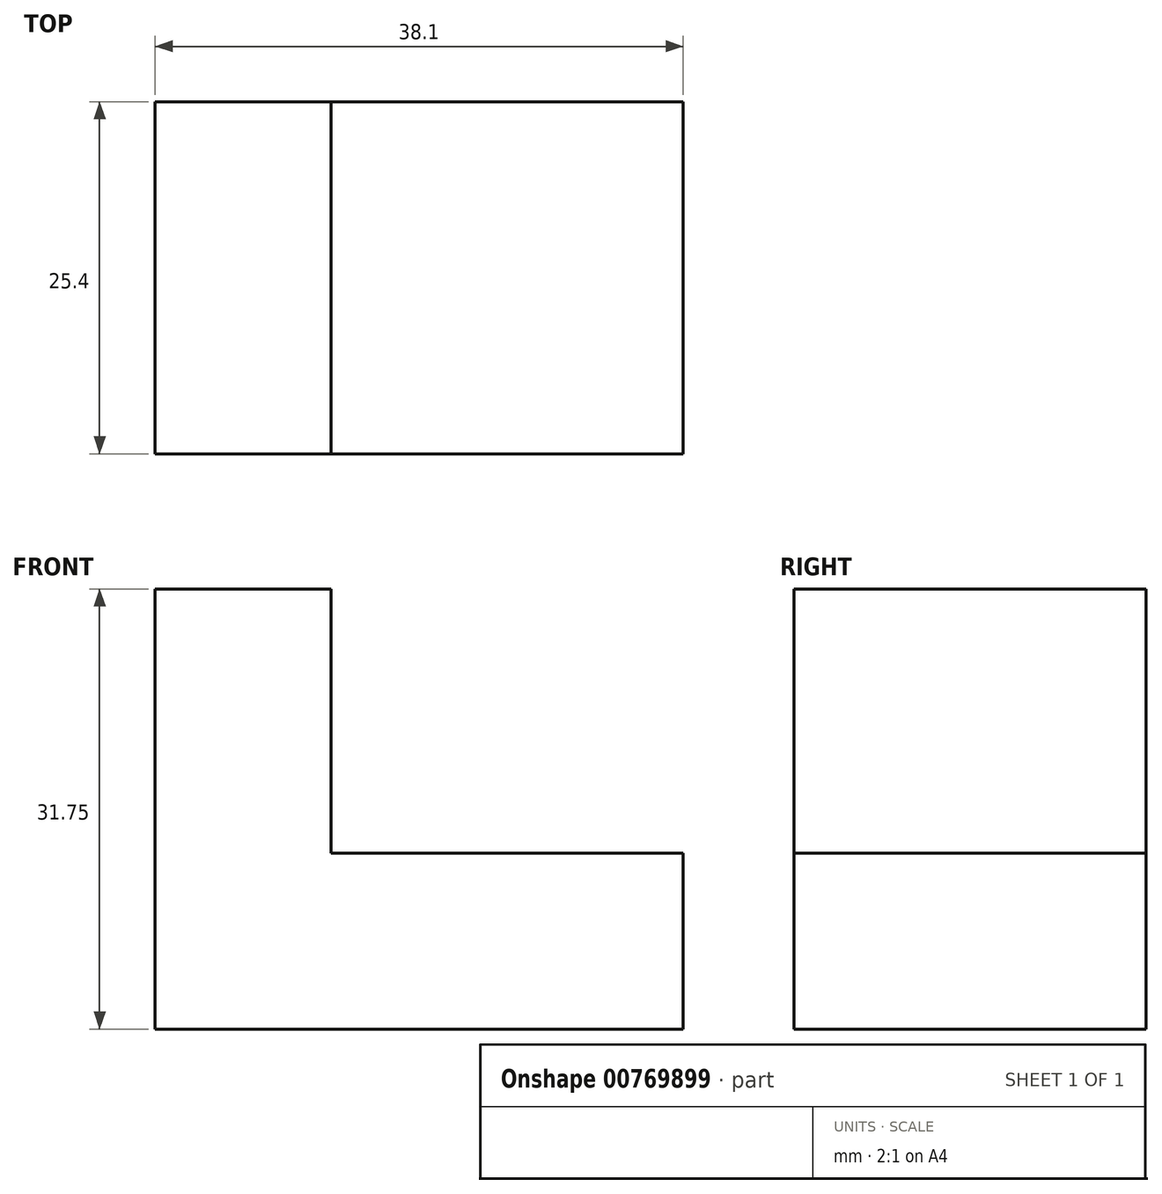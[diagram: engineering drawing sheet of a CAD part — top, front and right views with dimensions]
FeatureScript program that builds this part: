
annotation { "Feature Type Name" : "Feature", "Feature Type Description" : "" }
export const myFeature = defineFeature(function(context is Context, id is Id, definition is map)
    precondition{}
    {
        {
            var Q0;
            Q0=qCreatedBy(makeId("Front.planeOp"),FACE);
            var sketch = newSketch(context, id + "F0", { "sketchPlane" : qUnion([Q0])});
            skLineSegment(sketch, "E0", {"start": v(0, 0) * mm, "end": v(0, 31.75) * mm});
            skLineSegment(sketch, "E1", {"start": v(0, 0) * mm, "end": v(38.1, 0) * mm});
            skLineSegment(sketch, "E2", {"start": v(0, 31.75) * mm, "end": v(12.7, 31.75) * mm});
            skLineSegment(sketch, "E3", {"start": v(38.1, 0) * mm, "end": v(38.1, 12.7) * mm});
            skLineSegment(sketch, "E4", {"start": v(38.1, 12.7) * mm, "end": v(12.7, 12.7) * mm});
            skLineSegment(sketch, "E5", {"start": v(12.7, 12.7) * mm, "end": v(12.7, 31.75) * mm});
            skSolve(sketch);
        }
        {
            var Q0;
            Q0=makeQuery(id+"F0.imprint","IMPRINT",FACE,{"disambiguationData":[TD([[makeQuery(id+"F0.imprint","IMPRINT",EDGE,{"derivedFrom":sQuery(id+"F0.wireOp",EDGE,"E0")}),-1.0]])]});
            extrude(context, id + "F1", {"entities" : qUnion([Q0]), "depth" : 25.4 * mm, "offsetDistance" : 25.4 * mm});
        }
    });
